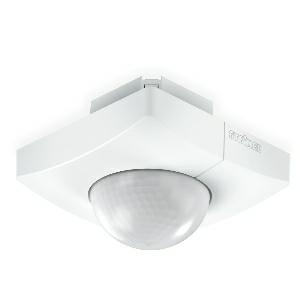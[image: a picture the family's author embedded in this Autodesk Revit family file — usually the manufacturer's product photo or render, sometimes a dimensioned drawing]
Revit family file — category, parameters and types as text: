
# Revit family: is_345_058265
name_source: partatom
category: Elektroinstallationen
revit_build: Autodesk Revit 2016 (Build: 20190508_0715(x64)
units: mm (PartAtom-declared; Revit-internal decimal feet)

## family parameters
Basisbauteil = Fläche
Beim Laden mit Abzugskörper schneiden = Nein
Bemaßung runder Anschluss = Durchmesser verwenden
Beschriftungsausrichtung beibehalten = Nein
Gemeinsam genutzt = Nein
Raumberechnungspunkt = Nein
Teiletyp = Normal

## types (1)
- IS 345
    Apparent Load = 0 VA
    Beschreibung = Type: Motion detectors; Dimensions (L x W x H): 78 x 94 x 94 mm; Sensor Technology: passive infrared; Application, place: Indoors; Application, room: corridor / aisle, multi-storey / underground car park, Indoors; Installation site: ceiling; Installation: Concealed wiring; Electronic scalability: No; Mechanical scalability: No; Mounting height: 2,50 – 5,00 m; Optimum mounting height: 2,5 m; Detection angle: 360 °; Angle of aperture: 45 °; Sneak-by guard: Yes; Capability of masking out individual segments: Yes; Reach, radial: 12 x 6 m (72 m²); Reach, tangential: 23 x 6 m (138 m²); Twilight setting TEACH: Yes; Time setting: 0 sec – 1092 min; Basic light level function: Yes; KNX functions: Photo-cell controller, Basic light level function, Light level, HVAC output, Constant-lighting control, Light output 2x, Presence output, Day / night function; With bus coupling: Yes; Settings via: ETS software, Remote control, Bus, Smart Remote; IP-rating: IP20; Material: Plastic; Colour: white; Version: KNX - concealed, sq.; PU1, EAN: 4007841058265
    Height = 0 mm  [stored 0 ft]
    Hersteller = Steinel
    Length = 78 mm  [stored 0.255906 ft]
    Maximum range = 11.589 m
    ModVariant = Nein
    Modell = 058265
    Mounting Place = Ceiling
    Mounting Type = Recessed
    Number of Poles = 1
    OnlyDefault = Ja
    Power Factor = 1
    Product Name = IS 345
    Product group = Presence detector
    ProductGroupID = 4
    Protection Class = Protection class
    Protection Degree = IP 20
    RlxData = <blob elided: 136909 chars, md5=0fb35428>
    Sensor characteristics = Stretched
    Sensor type = Passive (infrared)
    SensorDataFile = <blob elided: 5885 chars, md5=98bccc25>
    Type of entry = Motion
    Typenbild = produkt1_058265.jpg
    Typenkommentare = Product without accessories
    URL = http://relux.com
    VarID = ---
    Voltage = 0 V
    Vorgabe-Ansicht = 1800 mm
    Weight = 0.00 kg
    Width = 94 mm  [stored 0.308399 ft]

note: [stored X ft] marks values corroborated as IEEE doubles in the binary element streams (Revit-internal decimal feet)

## geometry (parser evidence)
native form markers: Sweep x13
no freeform markers — native parametric forms only
